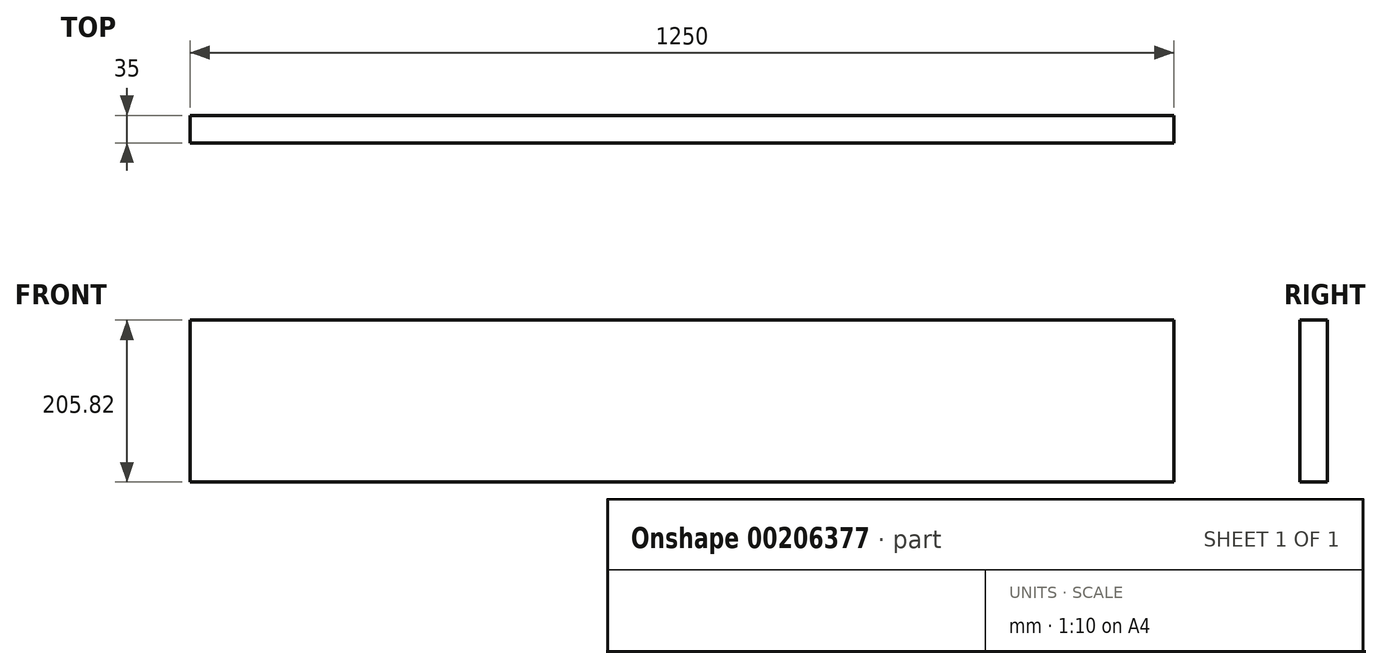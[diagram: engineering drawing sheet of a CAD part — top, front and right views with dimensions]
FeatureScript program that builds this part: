
annotation { "Feature Type Name" : "Feature", "Feature Type Description" : "" }
export const myFeature = defineFeature(function(context is Context, id is Id, definition is map)
    precondition{}
    {
        {
            var Q0;
            Q0=qCreatedBy(makeId("Front.planeOp"),FACE);
            var sketch = newSketch(context, id + "F0", { "sketchPlane" : qUnion([Q0])});
            skLineSegment(sketch, "E0.bottom", {"start": v(-100.6, -33.1) * mm, "end": v(99.4, -33.1) * mm});
            skLineSegment(sketch, "E0.top", {"start": v(-100.6, -38.9) * mm, "end": v(99.4, -38.9) * mm});
            skLineSegment(sketch, "E0.left", {"start": v(-100.6, -33.1) * mm, "end": v(-100.6, -38.9) * mm});
            skLineSegment(sketch, "E0.right", {"start": v(99.4, -33.1) * mm, "end": v(99.4, -38.9) * mm});
            skSolve(sketch);
        }
        {
            var Q0;
            Q0 = qSketchRegion(id + "F0", true);
            extrude(context, id + "F1", {"entities" : qUnion([Q0]), "depth" : 35 * mm});
        }
        {
            var Q0;
            Q0=makeQuery(id+"F1.opExtrude","SWEPT_FACE",FACE,{"disambiguationData":[OSD([sQuery(id+"F0.wireOp",EDGE,"E0.bottom")])]});
            extrude(context, id + "F2", {"entities" : qUnion([Q0]), "operationType" : NewBodyOperationType.ADD, "depth" : 200 * mm});
        }
        {
            var Q0;
            {var subQ0=sQuery(id+"F0.wireOp",EDGE,"E0.left");Q0=makeQuery(id+"F2.boolean.opBoolean","MERGE",FACE,{"derivedFrom":[makeQuery(id+"F1.opExtrude","SWEPT_FACE",FACE,{"disambiguationData":[OSD([subQ0])]}),makeQuery(id+"F2.opExtrude","SWEPT_FACE",FACE,{"disambiguationData":[OSD([sQuery(id+"F0.wireOp",EDGE,"E0.bottom"),subQ0])]})]});}
            extrude(context, id + "F3", {"entities" : qUnion([Q0]), "operationType" : NewBodyOperationType.ADD, "oppositeDirection" : true, "depth" : 1250 * mm});
        }
    });
